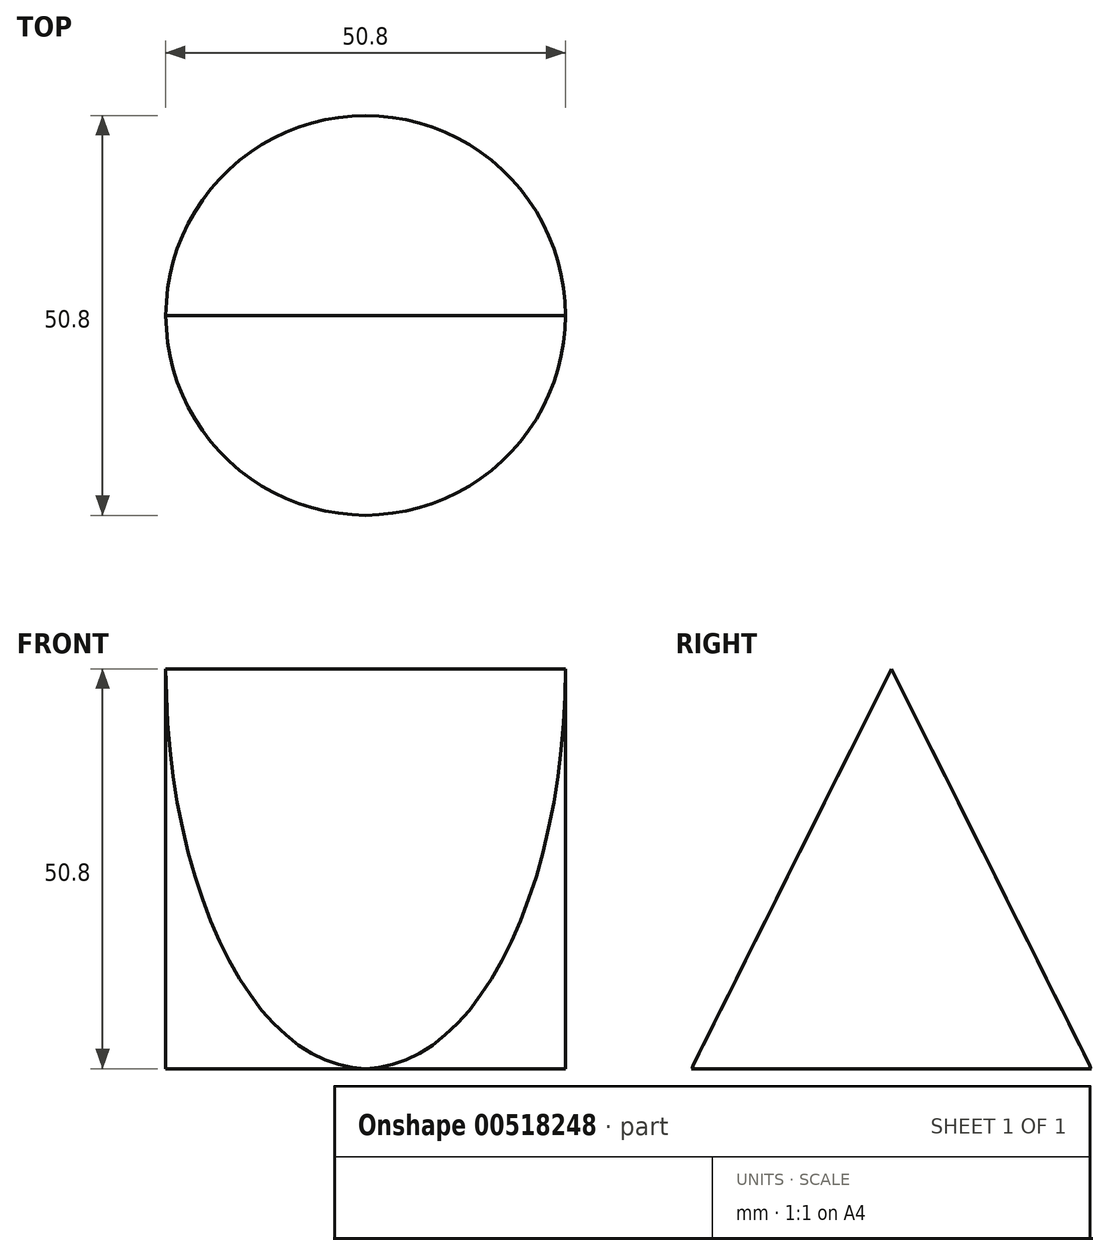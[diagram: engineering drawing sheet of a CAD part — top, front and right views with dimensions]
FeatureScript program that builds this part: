
annotation { "Feature Type Name" : "Feature", "Feature Type Description" : "" }
export const myFeature = defineFeature(function(context is Context, id is Id, definition is map)
    precondition{}
    {
        {
            var Q0;
            Q0=qCreatedBy(makeId("Top.planeOp"),FACE);
            var sketch = newSketch(context, id + "F0", { "sketchPlane" : qUnion([Q0])});
            skCircle(sketch, "E0", {"center": v(0, 0) * mm, "radius": 25.4 * mm});
            skSolve(sketch);
        }
        {
            var Q0;
            Q0=makeQuery(id+"F0.imprint","IMPRINT",FACE,{"disambiguationData":[TD([[makeQuery(id+"F0.imprint","IMPRINT",EDGE,{"derivedFrom":sQuery(id+"F0.wireOp",EDGE,"E0")}),1.0]])]});
            extrude(context, id + "F1", {"entities" : qUnion([Q0]), "depth" : 50.8 * mm, "offsetDistance" : 25.4 * mm});
        }
        {
            var Q0;
            Q0=qCreatedBy(makeId("Right.planeOp"),FACE);
            var sketch = newSketch(context, id + "F2", { "sketchPlane" : qUnion([Q0])});
            skLineSegment(sketch, "E1", {"start": v(-25.4, 0) * mm, "end": v(-25.4, 50.8) * mm});
            skLineSegment(sketch, "E2", {"start": v(25.4, 50.8) * mm, "end": v(25.4, 0) * mm});
            skLineSegment(sketch, "E3.0.0", {"start": v(-25.4, 50.8) * mm, "end": v(25.4, 50.8) * mm});
            skLineSegment(sketch, "E4.0", {"start": v(-25.4, 0) * mm, "end": v(25.4, 0) * mm});
            skLineSegment(sketch, "E5", {"start": v(0, 50.8) * mm, "end": v(-25.4, 0) * mm});
            skLineSegment(sketch, "E6", {"start": v(0, 50.8) * mm, "end": v(25.4, 0) * mm});
            skLineSegment(sketch, "E7", {"start": v(0, 50.8) * mm, "end": v(25.4, 50.8) * mm});
            skLineSegment(sketch, "E8", {"start": v(25.4, 0) * mm, "end": v(25.4, 50.8) * mm});
            skLineSegment(sketch, "E9", {"start": v(-25.4, 50.8) * mm, "end": v(0, 50.8) * mm});
            skLineSegment(sketch, "E10", {"start": v(-25.4, 50.8) * mm, "end": v(-25.4, 0) * mm});
            skSolve(sketch);
        }
        {
            var Q0;
            Q0=makeQuery(id+"F2.imprint","IMPRINT",FACE,{"disambiguationData":[TD([[makeQuery(id+"F2.imprint","IMPRINT",EDGE,{"derivedFrom":sQuery(id+"F2.wireOp",EDGE,"E5")}),-1.0]])]});
            var Q1;
            Q1=makeQuery(id+"F2.imprint","IMPRINT",FACE,{"disambiguationData":[TD([[makeQuery(id+"F2.imprint","IMPRINT",EDGE,{"derivedFrom":sQuery(id+"F2.wireOp",EDGE,"E6")}),1.0]])]});
            extrude(context, id + "F3", {"entities" : qUnion([Q0, Q1]), "operationType" : NewBodyOperationType.REMOVE, "endBound" : BoundingType.SYMMETRIC, "oppositeDirection" : true, "depth" : 50.8 * mm, "offsetDistance" : 25.4 * mm});
        }
    });
